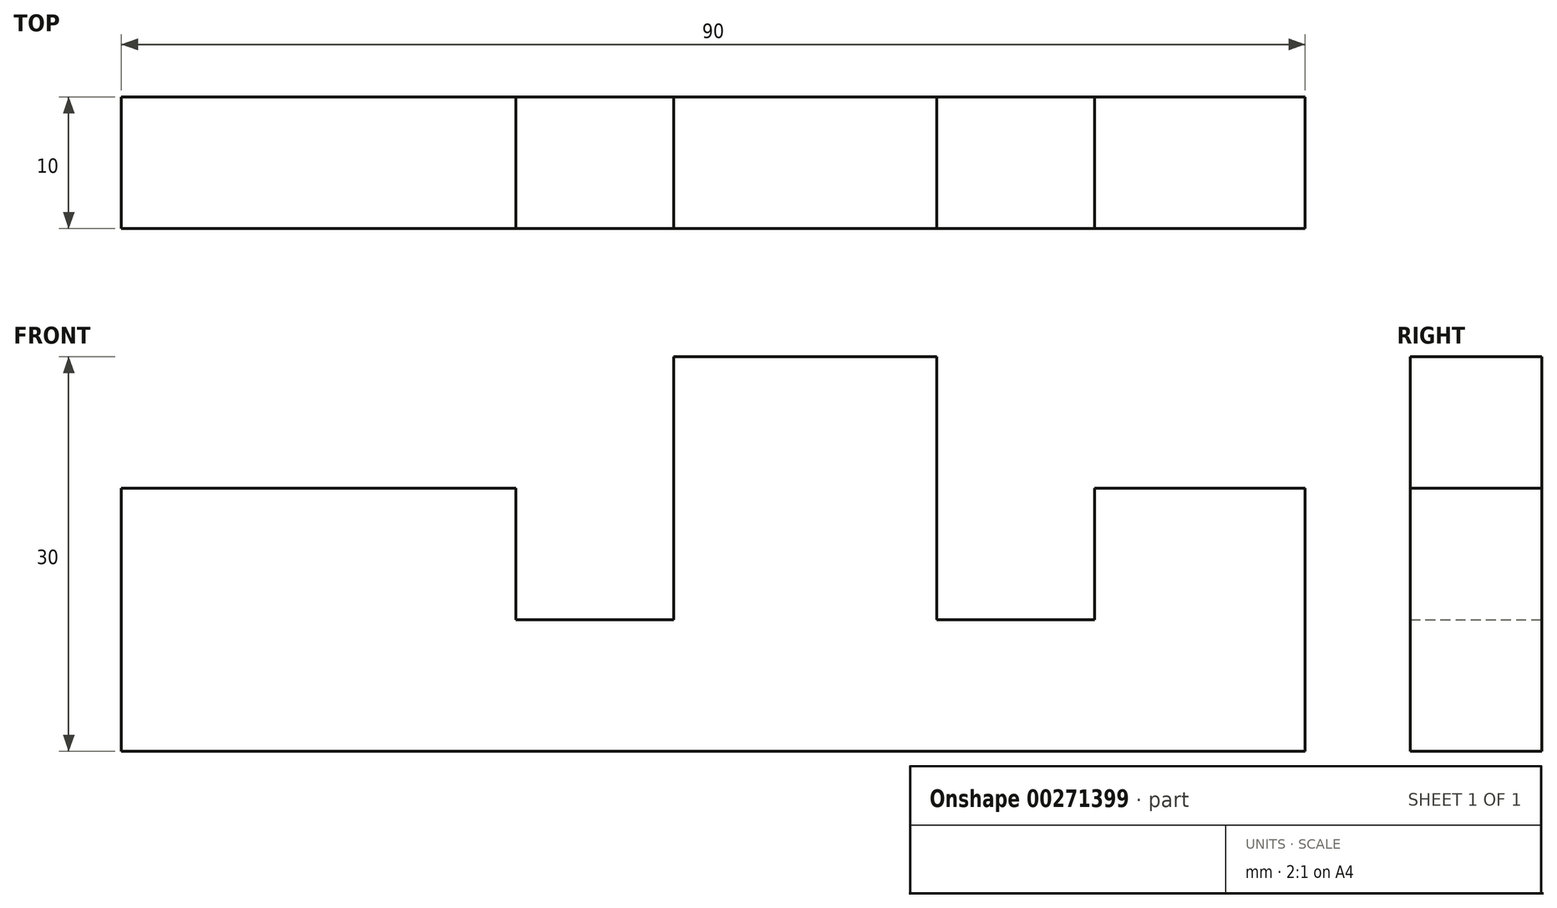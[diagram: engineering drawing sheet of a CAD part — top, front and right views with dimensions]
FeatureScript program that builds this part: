
annotation { "Feature Type Name" : "Feature", "Feature Type Description" : "" }
export const myFeature = defineFeature(function(context is Context, id is Id, definition is map)
    precondition{}
    {
        {
            var Q0;
            Q0=qCreatedBy(makeId("Front.planeOp"),FACE);
            var sketch = newSketch(context, id + "F0", { "sketchPlane" : qUnion([Q0])});
            skLineSegment(sketch, "E0", {"start": v(0, 0) * mm, "end": v(90, 0) * mm});
            skLineSegment(sketch, "E1", {"start": v(0, 0) * mm, "end": v(0, 20) * mm});
            skLineSegment(sketch, "E2", {"start": v(0, 20) * mm, "end": v(30, 20) * mm});
            skLineSegment(sketch, "E3", {"start": v(30, 10) * mm, "end": v(30, 20) * mm});
            skLineSegment(sketch, "E4", {"start": v(30, 10) * mm, "end": v(42, 10) * mm});
            skLineSegment(sketch, "E5", {"start": v(42, 10) * mm, "end": v(42, 30) * mm});
            skLineSegment(sketch, "E6", {"start": v(42, 30) * mm, "end": v(62, 30) * mm});
            skLineSegment(sketch, "E7", {"start": v(62, 30) * mm, "end": v(62, 10) * mm});
            skLineSegment(sketch, "E8", {"start": v(62, 10) * mm, "end": v(74, 10) * mm});
            skLineSegment(sketch, "E9", {"start": v(74, 10) * mm, "end": v(74, 20) * mm});
            skLineSegment(sketch, "E10", {"start": v(74, 20) * mm, "end": v(90, 20) * mm});
            skLineSegment(sketch, "E11", {"start": v(90, 20) * mm, "end": v(90, 0) * mm});
            skSolve(sketch);
        }
        {
            var Q0;
            Q0 = qSketchRegion(id + "F0", true);
            extrude(context, id + "F1", {"entities" : qUnion([Q0]), "depth" : 10 * mm});
        }
    });
